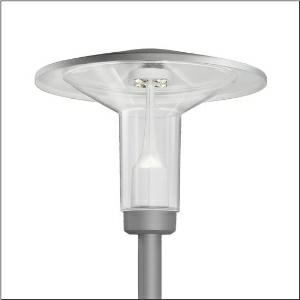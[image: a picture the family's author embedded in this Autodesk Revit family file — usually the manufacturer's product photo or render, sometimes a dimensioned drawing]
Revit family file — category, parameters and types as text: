
# Revit family: laterne_iq___st1_2a_5xa5255af14h_83bc
name_source: partatom
category: Lighting Fixtures
units: mm (PartAtom-declared; Revit-internal decimal feet)

## family parameters
Cut with Voids When Loaded = No
Host = Face
Light Source = No
Part Type = Normal
Room Calculation Point = No
Round Connector Dimension = Use Diameter
Shared = No

## types (1)
- --- (1 x LED, 1540 lm, 12.9 W, 2200K)
    Apparent Load = 13 VA
    CIE Flux Codes = 25 63 94 98 100
    Color Rendering = 70
    Color Temperature = 2200K
    Default Elevation = 1800 mm
    Description = Lantern iQ, mast luminaire, Module 540 iQ-SR, primary light control with 3 zone facetted reflector, of plastic, silver coated, highly specular, structured, primary optical cover: cover, of PMMA, transparent, light distribution: ST1.2a, light emission: direct distribution, primary light characteristic: asymmetric, installation type: post-top, LED, High Power LED, rated luminous flux: 1.540lm, luminous efficacy: 119lm/W, light colour: 722, colour temperature: 2200K, control gear: iQ Street-Remote, control: pre-setting: logarithmic dimming characteristic, Street-Remote, Auto-Match, Temp-Guard, Lumen-Switch, Night-Set, Smart-Wire, Light-Fading, Desk-Remote (wireless, voltage-free reading and setting of iQ features in the workshop via application-optimized NFC function/RFID function), optimised constant luminous flux control (CLO 2.0), with terminal, 6-pole, max. 2.5mm², mains connection: 230..240V, AC, 50/60Hz, start of lifetime: 13W, end of service life: 13W, reduction: 6W, luminaire housing, upper part, of glass-fibre reinforced polyester, coated, Siteco® metallic grey (DB 702S), diameter: 750mm, height: 583mm, spigot size: d x l = 76 x 70mm (post-top) | with reducer (optional accessory) 60 x 70mm, mounting height: 3..5m, post-top mast mounting element, of diecast aluminium, coated, Siteco® metallic grey (DB 702S), Module 540 iQ-SR, traffic white (RAL 9016), equipment: standard, protection rating (complete): IP65, insulation class (complete): insulation class II (safety insulation), certification: CE, ENEC, VDE, packaging unit: 1 piece

Light Distribution: ST1.2a
    Height = 583 mm
    Lamp = 1 x LED
    Lamp Light Flux = 1540 lm
    Lamp Power = 12.9 W
    Lamp count = 1
    Length = 750 mm
    Luminous efficacy = 119 lm/W
    Manufacturer = Siteco
    ModVariant = No
    Model = 5XA5255AF14H
    Number of Poles = 1
    OnlyDefault = Yes
    Power Factor = 1
    Product Name = Laterne iQ | ST1.2a
    Product group = mast luminaire | pylon top
    ProductGroupID = 6100
    Protection Class = Protection class II
    Protection Degree = IP 65
    RLX_Detail_Level = 1
    RLX_Emergency_Light_Flux = 0 lm
    RLX_Emergency_Type = 0
    RLX_Emergency_Type_DB = No
    RlxData = <blob elided: 103937 chars, md5=7d63dabe>
    Socket = socket
    Standby Power = 0 W
    System Light Flux = 1540 lm
    System Power = 13 W
    Type Comments = factory setting: luminous flux: 100 % | dim-lin: 254 | 516 mA
    Type Image = l_1006050.jpg
    URL = http://relux.com
    VarID = @adj_160145
    Voltage = 0 V
    Weight = 0.00 kg
    Width = 0 mm  [stored 0 ft]

note: [stored X ft] marks values corroborated as IEEE doubles in the binary element streams (Revit-internal decimal feet)

## geometry (parser evidence)
native form markers: Blend x4, Sweep x9
no freeform markers — native parametric forms only
